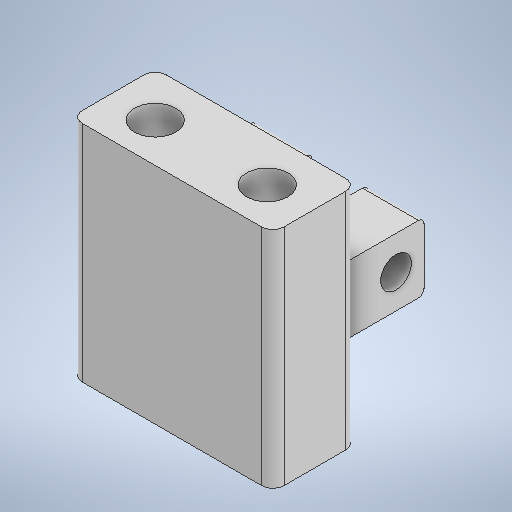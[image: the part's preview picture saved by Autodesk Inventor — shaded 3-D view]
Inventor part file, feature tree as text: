
AUTODESK INVENTOR PART (.ipt)
format: ipt  version: 2025.2 (Build 292293000, 293)  size: 328,192 bytes
history: native  units: mm
features: sketch x6, extrude x5, fillet x4, mirror x3, other x1, hole x1
ambient origin geometry x8: Origin, YZ Plane, XZ Plane, XY Plane, X Axis, Y Axis, Z Axis, Center Point
bodies: Body1 (feature_tree)
feature tree (20):
  other  "Bryła1"
  extrude  "Wyciągnięcie proste1"  Depth=40.0mm
  sketch  "Szkic3"
  fillet  "Zaokrąglenie1"  Radius=15.0mm
  extrude  "Wyciągnięcie proste3"  Depth=20.0mm TaperAngle=0.0deg
  extrude  "Wyciągnięcie proste4"  Depth=36.0mm
  extrude  "Wyciągnięcie proste6"  Depth=15.0mm
  mirror  "Odbij1"
  hole  "Otwór1"  [1 undecoded]
  mirror  "Odbij2"
  extrude  "Wyciągnięcie proste7"  Depth=8.0mm
  mirror  "Odbij3"
  fillet  "Zaokrąglenie4"  Radius=8.0mm
  fillet  "Zaokrąglenie5"  Radius=12.0mm
  fillet  "Zaokrąglenie6"  Radius=8.0mm
  sketch  "Szkic2"
  sketch  "Szkic4"
  sketch  "Szkic7"
  sketch  "Szkic10"
  sketch  "Szkic11"
note: 1 required parameter value undecoded (feature->parameter linkage not recoverable at this tier; creation-order binding heuristic only, values carry confidence <= 0.55)
